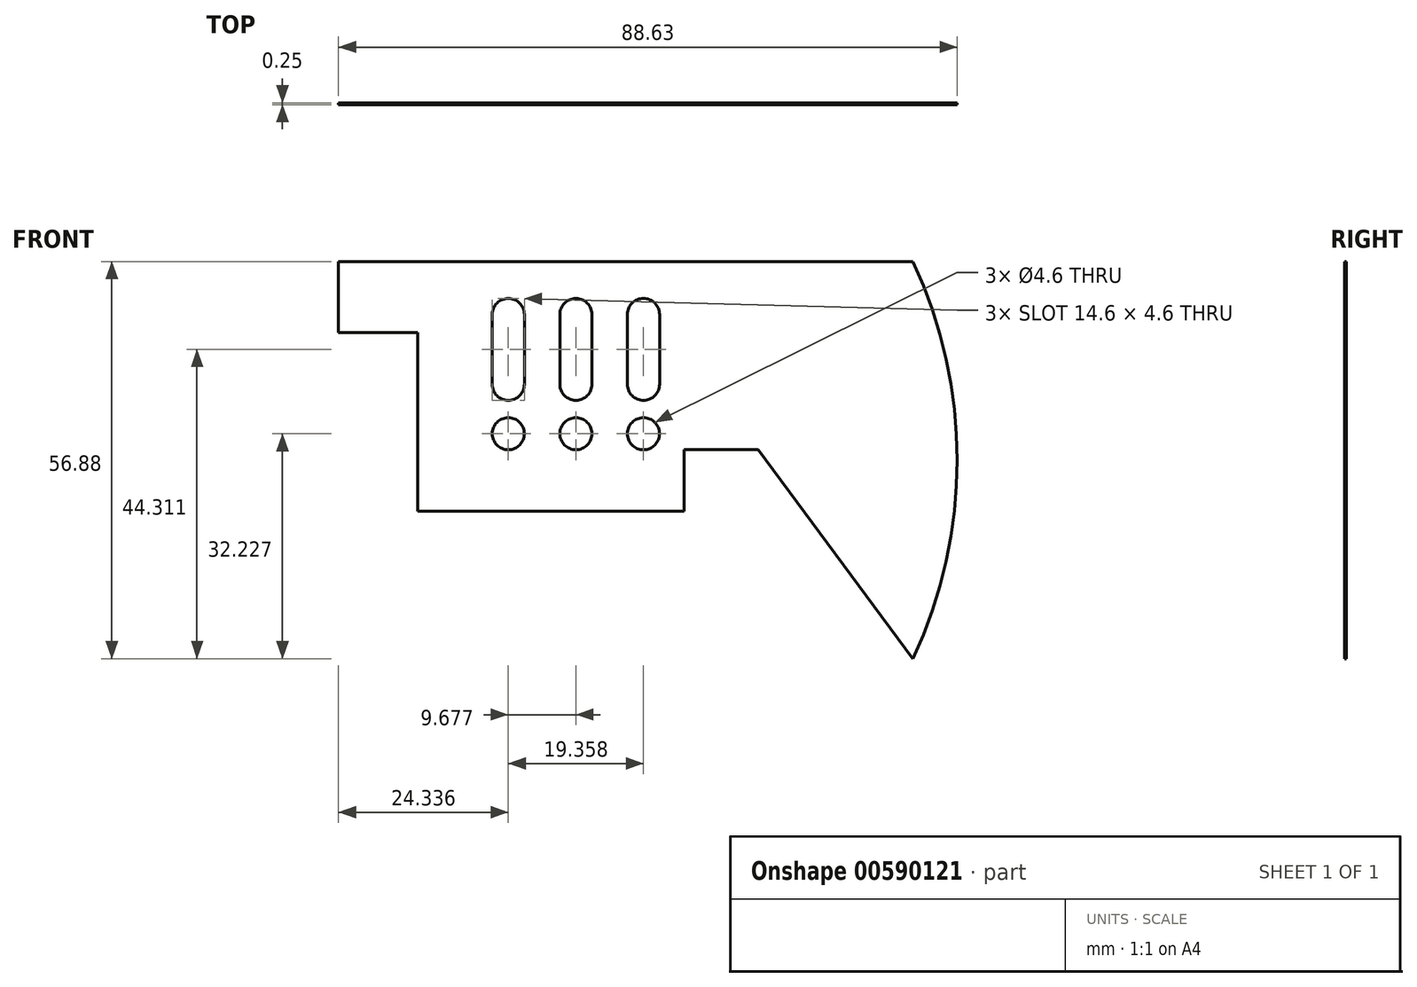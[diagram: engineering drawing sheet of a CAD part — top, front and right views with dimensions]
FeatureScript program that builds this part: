
annotation { "Feature Type Name" : "Feature", "Feature Type Description" : "" }
export const myFeature = defineFeature(function(context is Context, id is Id, definition is map)
    precondition{}
    {
        {
            var Q0;
            Q0=qCreatedBy(makeId("Front.planeOp"),FACE);
            var sketch = newSketch(context, id + "F0", { "sketchPlane" : qUnion([Q0])});
            skLineSegment(sketch, "E0", {"start": v(-58, 35.73) * mm, "end": v(-58, 25.57) * mm});
            skLineSegment(sketch, "E1", {"start": v(-58, 35.73) * mm, "end": v(24.32, 35.73) * mm});
            skLineSegment(sketch, "E2", {"start": v(-8.5, 8.78) * mm, "end": v(2.16, 8.78) * mm});
            skLineSegment(sketch, "E3", {"start": v(2.16, 8.78) * mm, "end": v(24.32, -21.15) * mm});
            skArc(sketch, "E4", {"start": v(24.32, -21.15) * mm, "mid": v(30.64, 7.29) * mm, "end": v(24.32, 35.73) * mm});
            skLineSegment(sketch, "E5", {"start": v(-58, 25.57) * mm, "end": v(-46.65, 25.57) * mm});
            skLineSegment(sketch, "E6", {"start": v(-46.65, 25.57) * mm, "end": v(-46.65, 0) * mm});
            skLineSegment(sketch, "E7", {"start": v(-46.65, 0) * mm, "end": v(-8.5, 0) * mm});
            skLineSegment(sketch, "E8", {"start": v(-8.5, 8.78) * mm, "end": v(-8.5, 0) * mm});
            skSolve(sketch);
        }
        {
            var Q0;
            Q0 = qSketchRegion(id + "F0", true);
            extrude(context, id + "F1", {"entities" : qUnion([Q0]), "depth" : 0.25 * mm, "offsetDistance" : 25.4 * mm});
        }
        {
            var Q0;
            Q0=makeQuery(id+"F1.opExtrude","CAP_FACE",FACE,{"disambiguationData":[OSD([sQuery(id+"F0.wireOp",EDGE,"E0"),sQuery(id+"F0.wireOp",EDGE,"7T1h6bRM-u6b7-nEJe-YpZF-Du2gyElvbqLj"),sQuery(id+"F0.wireOp",EDGE,"E1"),sQuery(id+"F0.wireOp",EDGE,"wXVbRxHJ-J3GY-TaMU-pPde-X8dqrCMW9NrD"),sQuery(id+"F0.wireOp",EDGE,"HZpDGVMu-4eV0-1fQT-ZMvl-6PiSzq7ffLmD"),sQuery(id+"F0.wireOp",EDGE,"E2"),sQuery(id+"F0.wireOp",EDGE,"E3"),sQuery(id+"F0.wireOp",EDGE,"E4")])],"isStart":true});
            var sketch = newSketch(context, id + "F2", { "sketchPlane" : qUnion([Q0])});
            skLineSegment(sketch, "E9", {"start": v(12, 28.16) * mm, "end": v(12, 18.16) * mm});
            skLineSegment(sketch, "E10", {"start": v(16.6, 28.16) * mm, "end": v(16.6, 18.16) * mm});
            skLineSegment(sketch, "E11", {"start": v(21.68, 28.16) * mm, "end": v(21.68, 18.16) * mm});
            skLineSegment(sketch, "E12", {"start": v(26.28, 18.16) * mm, "end": v(26.28, 28.16) * mm});
            skLineSegment(sketch, "E13", {"start": v(31.36, 28.16) * mm, "end": v(31.36, 18.16) * mm});
            skLineSegment(sketch, "E14", {"start": v(35.95, 18.16) * mm, "end": v(35.95, 28.16) * mm});
            skArc(sketch, "E15", {"start": v(16.6, 28.16) * mm, "mid": v(14.3, 30.46) * mm, "end": v(12, 28.16) * mm});
            skArc(sketch, "E16", {"start": v(12, 18.16) * mm, "mid": v(14.3, 15.86) * mm, "end": v(16.6, 18.16) * mm});
            skArc(sketch, "E17", {"start": v(21.68, 18.16) * mm, "mid": v(23.98, 15.86) * mm, "end": v(26.28, 18.16) * mm});
            skArc(sketch, "E18", {"start": v(26.28, 28.16) * mm, "mid": v(23.98, 30.46) * mm, "end": v(21.68, 28.16) * mm});
            skArc(sketch, "E19", {"start": v(35.95, 28.16) * mm, "mid": v(33.65, 30.46) * mm, "end": v(31.36, 28.16) * mm});
            skArc(sketch, "E20", {"start": v(31.36, 18.16) * mm, "mid": v(33.65, 15.86) * mm, "end": v(35.95, 18.16) * mm});
            skCircle(sketch, "E21", {"center": v(23.98, 11.08) * mm, "radius": 2.3 * mm});
            skCircle(sketch, "E22", {"center": v(14.3, 11.08) * mm, "radius": 2.3 * mm});
            skCircle(sketch, "E23", {"center": v(33.65, 11.08) * mm, "radius": 2.3 * mm});
            skPoint(sketch, "E23.centerSnap0", {"position": v(33.65, 15.86) * mm});
            skSolve(sketch);
        }
        {
            var Q0;
            Q0 = qSketchRegion(id + "F2", true);
            extrude(context, id + "F3", {"entities" : qUnion([Q0]), "operationType" : NewBodyOperationType.REMOVE, "oppositeDirection" : true, "depth" : 25.4 * mm, "offsetDistance" : 25.4 * mm});
        }
    });
